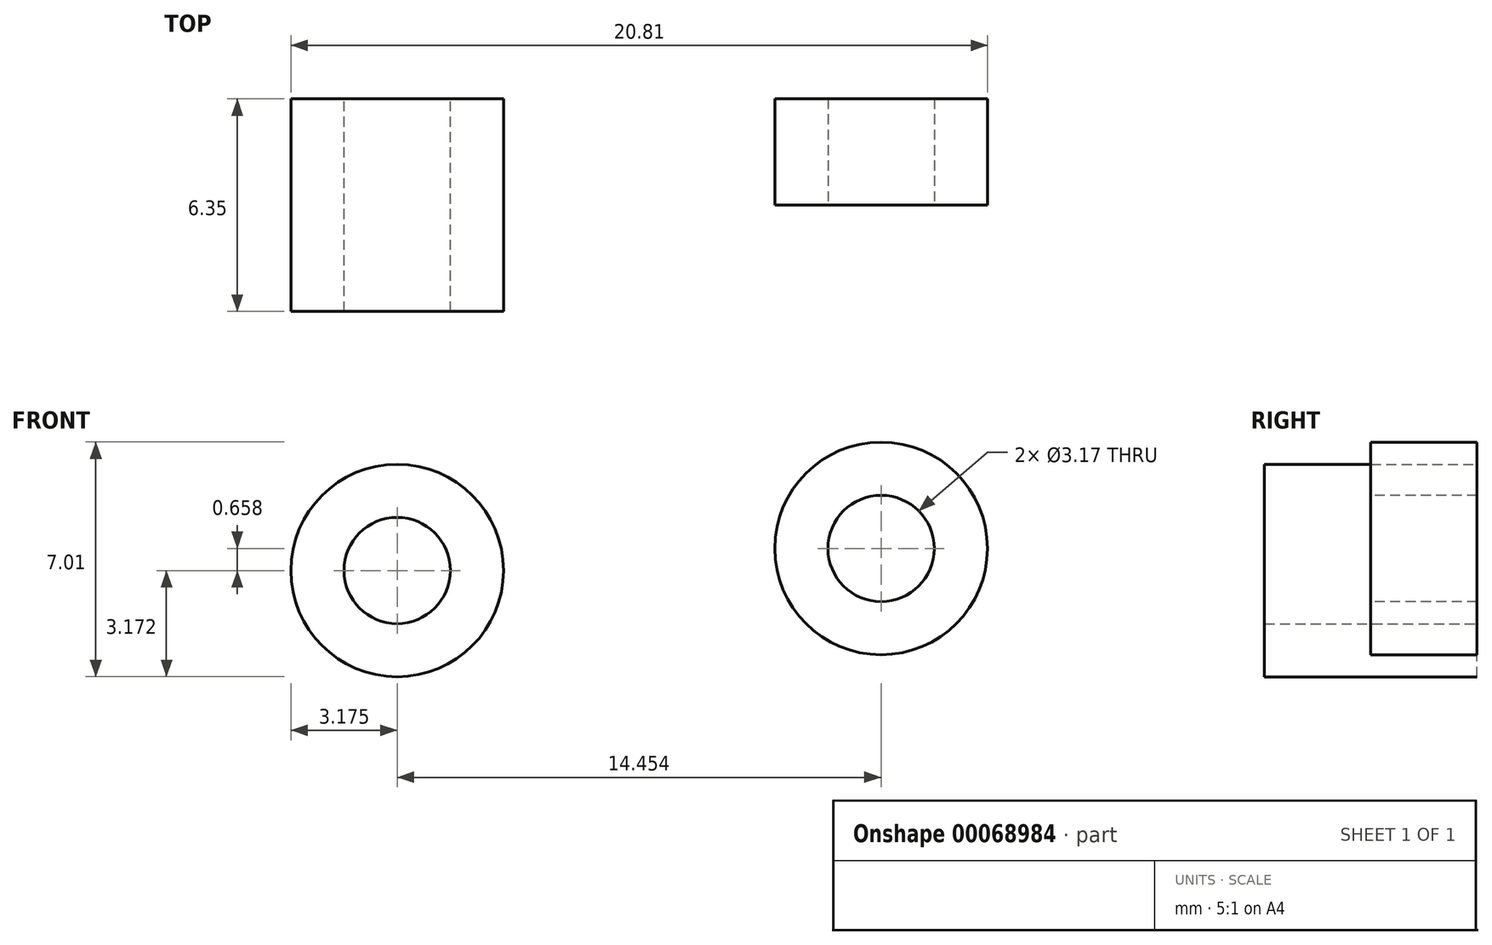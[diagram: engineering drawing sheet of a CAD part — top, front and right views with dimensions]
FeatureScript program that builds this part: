
annotation { "Feature Type Name" : "Feature", "Feature Type Description" : "" }
export const myFeature = defineFeature(function(context is Context, id is Id, definition is map)
    precondition{}
    {
        {
            var Q0;
            Q0=qCreatedBy(makeId("Front.planeOp"),FACE);
            var sketch = newSketch(context, id + "F0", { "sketchPlane" : qUnion([Q0])});
            skCircle(sketch, "E0", {"center": v(0, 0) * mm, "radius": 3.17 * mm});
            skCircle(sketch, "E1", {"center": v(-14.45, -0.66) * mm, "radius": 3.18 * mm});
            skCircle(sketch, "E2", {"center": v(-14.45, -0.66) * mm, "radius": 1.59 * mm});
            skSolve(sketch);
        }
        {
            var Q0;
            Q0 = qSketchRegion(id + "F0", true);
            extrude(context, id + "F1", {"entities" : qUnion([Q0]), "depth" : 3.17 * mm});
        }
        {
            var Q0;
            Q0=makeQuery(id+"F1.opExtrude","CAP_FACE",FACE,{"disambiguationData":[OSD([sQuery(id+"F0.wireOp",EDGE,"E0")])],"isStart":false});
            var sketch = newSketch(context, id + "F2", { "sketchPlane" : qUnion([Q0])});
            skCircle(sketch, "E3", {"center": v(0, 0) * mm, "radius": 1.59 * mm});
            skSolve(sketch);
        }
        {
            var Q0;
            Q0=makeQuery(id+"F2.imprint","IMPRINT",FACE,{"disambiguationData":[TD([[makeQuery(id+"F2.imprint","IMPRINT",EDGE,{"derivedFrom":sQuery(id+"F2.wireOp",EDGE,"E3")}),1.0]])]});
            extrude(context, id + "F3", {"entities" : qUnion([Q0]), "operationType" : NewBodyOperationType.REMOVE, "endBound" : BoundingType.THROUGH_ALL, "oppositeDirection" : true, "depth" : 25.4 * mm});
        }
        {
            var Q0;
            Q0=makeQuery(id+"F1.opExtrude","CAP_FACE",FACE,{"disambiguationData":[OSD([sQuery(id+"F0.wireOp",EDGE,"E1"),sQuery(id+"F0.wireOp",EDGE,"E2")])],"isStart":false});
            extrude(context, id + "F4", {"entities" : qUnion([Q0]), "operationType" : NewBodyOperationType.ADD, "depth" : 3.17 * mm});
        }
    });
